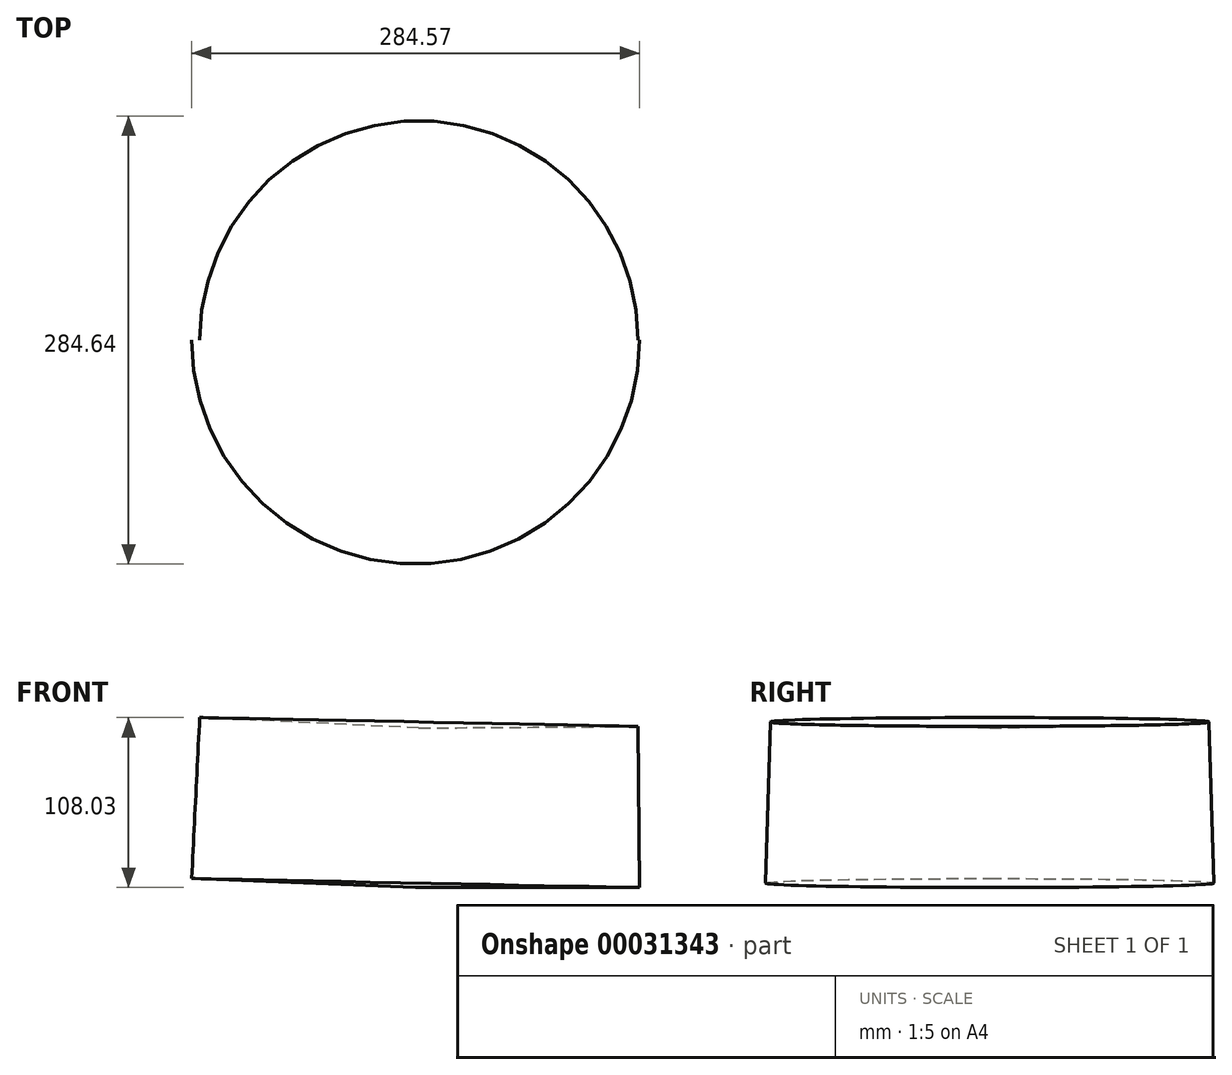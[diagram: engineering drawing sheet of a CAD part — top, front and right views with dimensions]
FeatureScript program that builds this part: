
annotation { "Feature Type Name" : "Feature", "Feature Type Description" : "" }
export const myFeature = defineFeature(function(context is Context, id is Id, definition is map)
    precondition{}
    {
        {
            var Q0;
            Q0=qCreatedBy(makeId("Front.planeOp"),FACE);
            var sketch = newSketch(context, id + "F0", { "sketchPlane" : qUnion([Q0])});
            skLineSegment(sketch, "E0", {"start": v(-138.25, 100.36) * mm, "end": v(140.3, 102.4) * mm});
            skLineSegment(sketch, "E1", {"start": v(140.3, 102.4) * mm, "end": v(142.34, -102.4) * mm});
            skLineSegment(sketch, "E2", {"start": v(142.34, -102.4) * mm, "end": v(-136.2, -102.4) * mm});
            skLineSegment(sketch, "E3", {"start": v(-136.2, -102.4) * mm, "end": v(-142.34, -102.4) * mm});
            skLineSegment(sketch, "E4", {"start": v(-142.34, -102.4) * mm, "end": v(-138.25, 100.36) * mm});
            skSolve(sketch);
        }
        {
            var Q0;
            Q0=makeQuery(id+"F0.imprint","IMPRINT",FACE,{"disambiguationData":[TD([[makeQuery(id+"F0.imprint","IMPRINT",EDGE,{"derivedFrom":sQuery(id+"F0.wireOp",EDGE,"E0")}),-1.0]])]});
            var Q1;
            Q1=sQuery(id+"F0.wireOp",EDGE,"E4");
            revolve(context, id + "F1", {"entities" : qUnion([Q0]), "axis" : qUnion([Q1]), "revolveType" : RevolveType.FULL});
        }
        {
            var Q0;
            Q0=makeQuery(id+"F1.opRevolve","SWEPT_BODY",BODY,{"disambiguationData":[OSD([sQuery(id+"F0.wireOp",EDGE,"E0"),sQuery(id+"F0.wireOp",EDGE,"E1"),sQuery(id+"F0.wireOp",EDGE,"E2"),sQuery(id+"F0.wireOp",EDGE,"E3"),sQuery(id+"F0.wireOp",EDGE,"E4")])]});
            transform(context, id + "F2", {"entities" : qUnion([Q0]), "transformType" : TransformType.TRANSLATION_3D, "dx" : 0 * mm, "dy" : 0 * mm, "dz" : 132 * mm, "makeCopy" : false});
        }
        {
            var Q0;
            Q0=makeQuery(id+"F1.opRevolve","SWEPT_BODY",BODY,{"disambiguationData":[OSD([sQuery(id+"F0.wireOp",EDGE,"E0"),sQuery(id+"F0.wireOp",EDGE,"E1"),sQuery(id+"F0.wireOp",EDGE,"E2"),sQuery(id+"F0.wireOp",EDGE,"E3"),sQuery(id+"F0.wireOp",EDGE,"E4")])]});
            var Q1;
            Q1=qCreatedBy(makeId("Origin.pointOp"),VERTEX);
            transform(context, id + "F3", {"entities" : qUnion([Q0]), "transformType" : TransformType.SCALE_UNIFORMLY, "scale" : .5, "makeCopy" : false, "scalePoint" : qUnion([Q1])});
        }
    });
